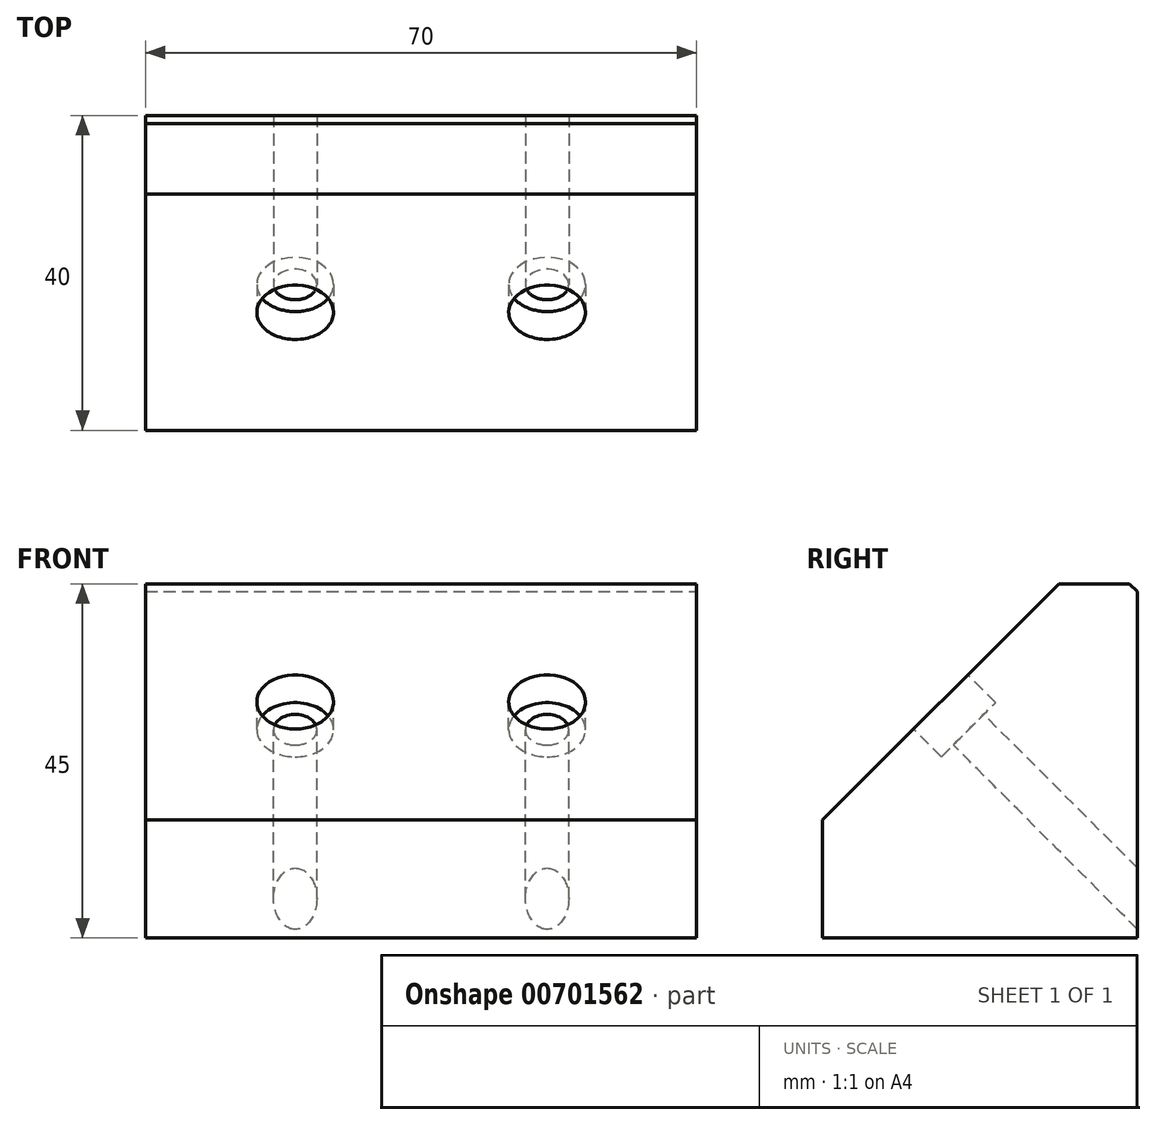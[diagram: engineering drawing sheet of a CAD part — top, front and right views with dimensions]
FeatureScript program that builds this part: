
annotation { "Feature Type Name" : "Feature", "Feature Type Description" : "" }
export const myFeature = defineFeature(function(context is Context, id is Id, definition is map)
    precondition{}
    {
        {
            var Q0;
            Q0=qCreatedBy(makeId("Top.planeOp"),FACE);
            var sketch = newSketch(context, id + "F0", { "sketchPlane" : qUnion([Q0])});
            skLineSegment(sketch, "E0.bottom", {"start": v(-101.79, -14.85) * mm, "end": v(-31.79, -14.85) * mm});
            skLineSegment(sketch, "E0.top", {"start": v(-101.79, -54.85) * mm, "end": v(-31.79, -54.85) * mm});
            skLineSegment(sketch, "E0.left", {"start": v(-101.79, -14.85) * mm, "end": v(-101.79, -54.85) * mm});
            skLineSegment(sketch, "E0.right", {"start": v(-31.79, -14.85) * mm, "end": v(-31.79, -54.85) * mm});
            skSolve(sketch);
        }
        {
            var Q0;
            Q0 = qSketchRegion(id + "F0", true);
            extrude(context, id + "F1", {"entities" : qUnion([Q0]), "depth" : 45 * mm, "offsetDistance" : 25 * mm});
        }
        {
            var Q0;
            Q0=makeQuery(id+"F1.opExtrude","CAP_EDGE",EDGE,{"disambiguationData":[OSD([sQuery(id+"F0.wireOp",EDGE,"E0.top")])],"isStart":false});
            chamfer(context, id + "F2", {"entities" : qUnion([Q0]), "width" : 30 * mm, "tangentPropagation" : true});
        }
        {
            var Q0;
            Q0=makeQuery(id+"F2.opChamfer","BLEND_FACE",FACE,{"disambiguationData":[OSD([sQuery(id+"F0.wireOp",EDGE,"E0.top")])]});
            var sketch = newSketch(context, id + "F3", { "sketchPlane" : qUnion([Q0])});
            skPoint(sketch, "E1", {"position": v(-82.79, -6.97) * mm});
            skPoint(sketch, "E2", {"position": v(-50.79, -6.97) * mm});
            skSolve(sketch);
        }
        {
            var Q0;
            Q0=sQuery(id+"F3.wireOp",VERTEX,"E1");
            var Q1;
            Q1=sQuery(id+"F3.wireOp",VERTEX,"E2");
            var Q2;
            Q2=makeQuery(id+"F1.opExtrude","SWEPT_BODY",BODY,{"disambiguationData":[OSD([sQuery(id+"F0.wireOp",EDGE,"E0.bottom"),sQuery(id+"F0.wireOp",EDGE,"E0.top"),sQuery(id+"F0.wireOp",EDGE,"E0.left"),sQuery(id+"F0.wireOp",EDGE,"E0.right")])]});
            hole(context, id + "F4", {"style" : HoleStyle.C_BORE, "endStyle" : HoleEndStyle.THROUGH, "standardTappedOrClearance" : lookupTablePath({ "standard" : "ISO", "fit" : "Normal", "size" : "M5", "type" : "Clearance" }), "standardBlindInLast" : lookupTablePath({ "fit" : "Standard", "standard" : "ISO", "size" : "M5", "type" : "Clearance" }), "holeDiameter" : 5.5 * mm, "cBoreDiameter" : 9.75 * mm, "cBoreDepth" : 5 * mm, "majorDiameter" : 5 * mm, "isTappedThrough" : true, "tappedDepth" : 12 * mm, "tapClearance" : 3, "locations" : qUnion([Q0, Q1]), "scope" : qUnion([Q2])});
        }
        {
            var Q0;
            Q0=makeQuery(id+"F1.opExtrude","CAP_EDGE",EDGE,{"disambiguationData":[OSD([sQuery(id+"F0.wireOp",EDGE,"E0.bottom")])],"isStart":false});
            chamfer(context, id + "F5", {"entities" : qUnion([Q0]), "width" : 1 * mm, "tangentPropagation" : true});
        }
    });
